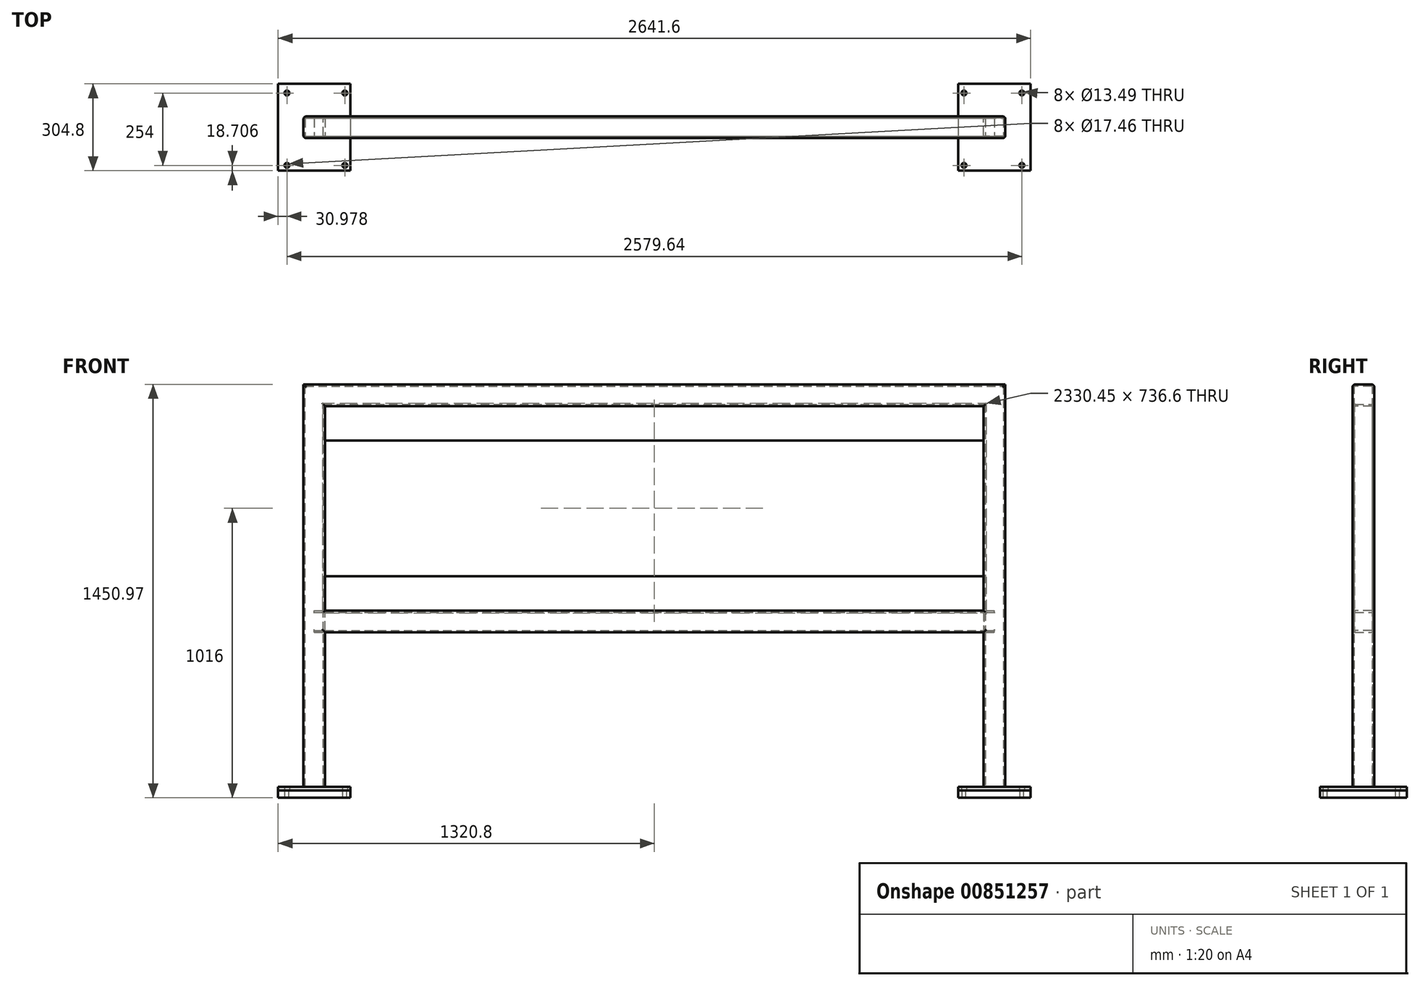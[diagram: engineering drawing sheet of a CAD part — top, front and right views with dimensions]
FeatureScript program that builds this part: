
annotation { "Feature Type Name" : "Feature", "Feature Type Description" : "" }
export const myFeature = defineFeature(function(context is Context, id is Id, definition is map)
    precondition{}
    {
        {
            var Q0;
            Q0=qCreatedBy(makeId("Top.planeOp"),FACE);
            var sketch = newSketch(context, id + "F0", { "sketchPlane" : qUnion([Q0])});
            skLineSegment(sketch, "E0", {"start": v(0, 315.7) * mm, "end": v(0, -421.09) * mm, "construction": true});
            skLineSegment(sketch, "E1", {"start": v(-1193.8, 0) * mm, "end": v(1193.8, 0) * mm, "construction": true});
            skLineSegment(sketch, "E2.0", {"start": v(-1193.8, 315.7) * mm, "end": v(-1193.8, -421.09) * mm, "construction": true});
            skPoint(sketch, "E3.orphan", {"position": v(-471.24, 0) * mm});
            skLineSegment(sketch, "E4.MirrorCS", {"start": v(1193.8, 315.7) * mm, "end": v(1193.8, -421.09) * mm, "construction": true});
            skLineSegment(sketch, "E5.bottom", {"start": v(-1320.8, 152.4) * mm, "end": v(-1066.8, 152.4) * mm});
            skLineSegment(sketch, "E5.top", {"start": v(-1320.8, -152.4) * mm, "end": v(-1066.8, -152.4) * mm});
            skLineSegment(sketch, "E5.left", {"start": v(-1320.8, 152.4) * mm, "end": v(-1320.8, -152.4) * mm});
            skLineSegment(sketch, "E5.right", {"start": v(-1066.8, 152.4) * mm, "end": v(-1066.8, -152.4) * mm});
            skPoint(sketch, "E5.middle", {"position": v(-1193.8, 0) * mm});
            skSolve(sketch);
        }
        {
            var Q0;
            Q0 = qSketchRegion(id + "F0", true);
            extrude(context, id + "F1", {"entities" : qUnion([Q0]), "depth" : 25.4 * mm, "offsetDistance" : 25.4 * mm});
        }
        {
            var Q0;
            Q0=makeQuery(id+"F1.opExtrude","CAP_FACE",FACE,{"disambiguationData":[OSD([sQuery(id+"F0.wireOp",EDGE,"E5.bottom"),sQuery(id+"F0.wireOp",EDGE,"E5.top"),sQuery(id+"F0.wireOp",EDGE,"E5.left"),sQuery(id+"F0.wireOp",EDGE,"E5.right")])],"isStart":false});
            var sketch = newSketch(context, id + "F2", { "sketchPlane" : qUnion([Q0])});
            skLineSegment(sketch, "E6", {"start": v(-1320.8, 152.4) * mm, "end": v(-1066.8, -152.4) * mm, "construction": true});
            skLineSegment(sketch, "E7.bottom", {"start": v(-1289.82, 120.3) * mm, "end": v(-1086.62, 120.3) * mm, "construction": true});
            skLineSegment(sketch, "E7.top", {"start": v(-1289.82, -133.7) * mm, "end": v(-1086.62, -133.7) * mm, "construction": true});
            skLineSegment(sketch, "E7.left", {"start": v(-1289.82, 120.3) * mm, "end": v(-1289.82, -133.7) * mm, "construction": true});
            skLineSegment(sketch, "E7.right", {"start": v(-1086.62, 120.3) * mm, "end": v(-1086.62, -133.7) * mm, "construction": true});
            skPoint(sketch, "E7.middle", {"position": v(-1188.22, -6.7) * mm});
            skPoint(sketch, "E8", {"position": v(-1289.82, 120.3) * mm});
            skPoint(sketch, "E9", {"position": v(-1086.62, 120.3) * mm});
            skPoint(sketch, "E10", {"position": v(-1289.82, -133.7) * mm});
            skPoint(sketch, "E11", {"position": v(-1086.62, -133.7) * mm});
            skSolve(sketch);
        }
        {
            var Q0;
            Q0=sQuery(id+"F2.wireOp",VERTEX,"E8");
            var Q1;
            Q1=sQuery(id+"F2.wireOp",VERTEX,"E9");
            var Q2;
            Q2=sQuery(id+"F2.wireOp",VERTEX,"E10");
            var Q3;
            Q3=sQuery(id+"F2.wireOp",VERTEX,"E11");
            var Q4;
            Q4=makeQuery(id+"F1.opExtrude","SWEPT_BODY",BODY,{"disambiguationData":[OSD([sQuery(id+"F0.wireOp",EDGE,"E5.bottom"),sQuery(id+"F0.wireOp",EDGE,"E5.top"),sQuery(id+"F0.wireOp",EDGE,"E5.left"),sQuery(id+"F0.wireOp",EDGE,"E5.right")])]});
            hole(context, id + "F3", {"style" : HoleStyle.SIMPLE, "endStyle" : HoleEndStyle.THROUGH, "standardTappedOrClearance" : lookupTablePath({ "standard" : "ANSI", "engagement" : "75%", "pitch" : "11 tpi", "size" : "5/8", "type" : "Tapped" }), "standardBlindInLast" : lookupTablePath({ "standard" : "ANSI", "engagement" : "75%", "pitch" : "11 tpi", "size" : "5/8", "type" : "Tapped" }), "holeDiameter" : 13.5 * mm, "majorDiameter" : 15.88 * mm, "showTappedDepth" : true, "isTappedThrough" : true, "tappedDepth" : 38.1 * mm, "tapClearance" : 3, "startFromSketch" : true, "locations" : qUnion([Q0, Q1, Q2, Q3]), "scope" : qUnion([Q4])});
        }
        {
            var Q0;
            Q0=makeQuery(id+"F1.opExtrude","CAP_FACE",FACE,{"disambiguationData":[OSD([sQuery(id+"F0.wireOp",EDGE,"E5.bottom"),sQuery(id+"F0.wireOp",EDGE,"E5.top"),sQuery(id+"F0.wireOp",EDGE,"E5.left"),sQuery(id+"F0.wireOp",EDGE,"E5.right")])],"isStart":false});
            var sketch = newSketch(context, id + "F4", { "sketchPlane" : qUnion([Q0])});
            skLineSegment(sketch, "E12.0", {"start": v(-1320.8, 152.4) * mm, "end": v(-1066.8, 152.4) * mm});
            skLineSegment(sketch, "E13.0", {"start": v(-1320.8, 152.4) * mm, "end": v(-1320.8, -152.4) * mm});
            skLineSegment(sketch, "E14.0", {"start": v(-1320.8, -152.4) * mm, "end": v(-1066.8, -152.4) * mm});
            skLineSegment(sketch, "E15.0", {"start": v(-1066.8, 152.4) * mm, "end": v(-1066.8, -152.4) * mm});
            skCircle(sketch, "E16.0", {"center": v(-1289.82, 120.3) * mm, "radius": 6.75 * mm, "construction": true});
            skCircle(sketch, "E17.0", {"center": v(-1086.62, 120.3) * mm, "radius": 6.75 * mm, "construction": true});
            skCircle(sketch, "E18.0", {"center": v(-1289.82, -133.7) * mm, "radius": 6.75 * mm, "construction": true});
            skCircle(sketch, "E19.0", {"center": v(-1086.62, -133.7) * mm, "radius": 6.75 * mm, "construction": true});
            skCircle(sketch, "E20", {"center": v(-1289.82, 120.3) * mm, "radius": 8.73 * mm});
            skCircle(sketch, "E21", {"center": v(-1086.62, 120.3) * mm, "radius": 8.73 * mm});
            skCircle(sketch, "E22", {"center": v(-1289.82, -133.7) * mm, "radius": 8.73 * mm});
            skCircle(sketch, "E23", {"center": v(-1086.62, -133.7) * mm, "radius": 8.73 * mm});
            skSolve(sketch);
        }
        {
            var Q0;
            Q0 = qSketchRegion(id + "F4", true);
            extrude(context, id + "F5", {"entities" : qUnion([Q0]), "depth" : 12.7 * mm, "offsetDistance" : 25.4 * mm});
        }
        {
            var Q0;
            Q0=makeQuery(id+"F5.opExtrude","SWEPT_BODY",BODY,{"disambiguationData":[OSD([sQuery(id+"F4.wireOp",EDGE,"E12.0"),sQuery(id+"F4.wireOp",EDGE,"E13.0"),sQuery(id+"F4.wireOp",EDGE,"E14.0"),sQuery(id+"F4.wireOp",EDGE,"E15.0"),sQuery(id+"F4.wireOp",EDGE,"E20"),sQuery(id+"F4.wireOp",EDGE,"E21"),sQuery(id+"F4.wireOp",EDGE,"E22"),sQuery(id+"F4.wireOp",EDGE,"E23")])]});
            var Q1;
            Q1=makeQuery(id+"F1.opExtrude","SWEPT_BODY",BODY,{"disambiguationData":[OSD([sQuery(id+"F0.wireOp",EDGE,"E5.bottom"),sQuery(id+"F0.wireOp",EDGE,"E5.top"),sQuery(id+"F0.wireOp",EDGE,"E5.left"),sQuery(id+"F0.wireOp",EDGE,"E5.right")])]});
            var Q2;
            Q2=qCreatedBy(makeId("Right.planeOp"),FACE);
            mirror(context, id + "F6", {"entities" : qUnion([Q0, Q1]), "mirrorPlane" : qUnion([Q2])});
        }
        {
            var Q0;
            Q0=qCreatedBy(makeId("Front.planeOp"),FACE);
            var sketch = newSketch(context, id + "F7", { "sketchPlane" : qUnion([Q0])});
            skLineSegment(sketch, "E24.0", {"start": v(-1320.8, 38.1) * mm, "end": v(-1066.8, 38.1) * mm, "construction": true});
            skLineSegment(sketch, "E25.0", {"start": v(1320.8, 38.1) * mm, "end": v(1066.8, 38.1) * mm, "construction": true});
            skLineSegment(sketch, "E26", {"start": v(-1193.8, 38.1) * mm, "end": v(-1193.8, 1412.88) * mm});
            skLineSegment(sketch, "E27", {"start": v(-1193.8, 1412.88) * mm, "end": v(1193.8, 1412.88) * mm});
            skPoint(sketch, "E27.endSnap0", {"position": v(1193.8, 38.1) * mm});
            skLineSegment(sketch, "E28", {"start": v(1193.8, 1412.88) * mm, "end": v(1193.8, 38.1) * mm});
            skLineSegment(sketch, "E29", {"start": v(1193.8, 581.03) * mm, "end": v(-1193.8, 581.02) * mm});
            skSolve(sketch);
        }
        {
            var Q0;
            Q0=makeQuery(id+"F5.opExtrude","CAP_FACE",FACE,{"disambiguationData":[OSD([sQuery(id+"F4.wireOp",EDGE,"E12.0"),sQuery(id+"F4.wireOp",EDGE,"E13.0"),sQuery(id+"F4.wireOp",EDGE,"E14.0"),sQuery(id+"F4.wireOp",EDGE,"E15.0"),sQuery(id+"F4.wireOp",EDGE,"E20"),sQuery(id+"F4.wireOp",EDGE,"E21"),sQuery(id+"F4.wireOp",EDGE,"E22"),sQuery(id+"F4.wireOp",EDGE,"E23")])],"isStart":false});
            var sketch = newSketch(context, id + "F8", { "sketchPlane" : qUnion([Q0])});
            skLineSegment(sketch, "E30.0", {"start": v(1193.8, 0) * mm, "end": v(-1193.8, 0) * mm, "construction": true});
            skLineSegment(sketch, "E31.bottom", {"start": v(-1222.38, 38.1) * mm, "end": v(-1165.23, 38.1) * mm});
            skLineSegment(sketch, "E31.top", {"start": v(-1222.38, -38.1) * mm, "end": v(-1165.23, -38.1) * mm});
            skLineSegment(sketch, "E31.left", {"start": v(-1231.9, 28.57) * mm, "end": v(-1231.9, -28.58) * mm});
            skLineSegment(sketch, "E31.right", {"start": v(-1155.7, 28.57) * mm, "end": v(-1155.7, -28.58) * mm});
            skPoint(sketch, "E31.middle", {"position": v(-1193.8, 0) * mm});
            skPoint(sketch, "E32.visualSharp", {"position": v(-1231.9, 38.1) * mm});
            skArc(sketch, "E32.filletArc", {"start": v(-1222.38, 38.1) * mm, "mid": v(-1229.11, 35.31) * mm, "end": v(-1231.9, 28.57) * mm});
            skPoint(sketch, "E33.visualSharp", {"position": v(-1155.7, 38.1) * mm});
            skArc(sketch, "E33.filletArc", {"start": v(-1155.7, 28.57) * mm, "mid": v(-1158.49, 35.31) * mm, "end": v(-1165.23, 38.1) * mm});
            skPoint(sketch, "E34.visualSharp", {"position": v(-1155.7, -38.1) * mm});
            skArc(sketch, "E34.filletArc", {"start": v(-1165.23, -38.1) * mm, "mid": v(-1158.49, -35.31) * mm, "end": v(-1155.7, -28.58) * mm});
            skPoint(sketch, "E35.visualSharp", {"position": v(-1231.9, -38.1) * mm});
            skArc(sketch, "E35.filletArc", {"start": v(-1231.9, -28.58) * mm, "mid": v(-1229.11, -35.31) * mm, "end": v(-1222.38, -38.1) * mm});
            skArc(sketch, "E36.0", {"start": v(-1222.38, 31.75) * mm, "mid": v(-1224.62, 30.82) * mm, "end": v(-1225.55, 28.57) * mm});
            skLineSegment(sketch, "E36.1", {"start": v(-1225.55, 28.57) * mm, "end": v(-1225.55, -28.58) * mm});
            skLineSegment(sketch, "E36.2", {"start": v(-1222.38, 31.75) * mm, "end": v(-1165.23, 31.75) * mm});
            skArc(sketch, "E36.3", {"start": v(-1225.55, -28.58) * mm, "mid": v(-1224.62, -30.82) * mm, "end": v(-1222.38, -31.75) * mm});
            skArc(sketch, "E36.4", {"start": v(-1162.05, 28.57) * mm, "mid": v(-1162.98, 30.82) * mm, "end": v(-1165.23, 31.75) * mm});
            skLineSegment(sketch, "E36.5", {"start": v(-1162.05, 28.57) * mm, "end": v(-1162.05, -28.58) * mm});
            skArc(sketch, "E36.6", {"start": v(-1165.23, -31.75) * mm, "mid": v(-1162.98, -30.82) * mm, "end": v(-1162.05, -28.58) * mm});
            skLineSegment(sketch, "E36.7", {"start": v(-1222.38, -31.75) * mm, "end": v(-1165.23, -31.75) * mm});
            skSolve(sketch);
        }
        {
            var Q0;
            Q0=makeQuery(id+"F8.imprint","IMPRINT",FACE,{"disambiguationData":[TD([[makeQuery(id+"F8.imprint","IMPRINT",EDGE,{"derivedFrom":sQuery(id+"F8.wireOp",EDGE,"E31.bottom")}),-1.0]])]});
            var Q1;
            Q1=sQuery(id+"F7.wireOp",EDGE,"E26");
            var Q2;
            Q2=sQuery(id+"F7.wireOp",EDGE,"E27");
            var Q3;
            Q3=sQuery(id+"F7.wireOp",EDGE,"E28");
            sweep(context, id + "F9", {"profiles" : qUnion([Q0]), "path" : qUnion([Q1, Q2, Q3])});
        }
        {
            var Q0;
            Q0=makeQuery(id+"F9.opSweep","SWEPT_FACE",FACE,{"disambiguationData":[OSD([sQuery(id+"F7.wireOp",EDGE,"E26"),sQuery(id+"F8.wireOp",EDGE,"E31.right")])]});
            var sketch = newSketch(context, id + "F10", { "sketchPlane" : qUnion([Q0])});
            skLineSegment(sketch, "E37.0", {"start": v(-28.58, 619.12) * mm, "end": v(28.57, 619.12) * mm, "construction": true});
            skLineSegment(sketch, "E38.bottom", {"start": v(28.57, 657.23) * mm, "end": v(-28.58, 657.23) * mm});
            skLineSegment(sketch, "E38.top", {"start": v(28.57, 581.02) * mm, "end": v(-28.58, 581.02) * mm});
            skLineSegment(sketch, "E38.left", {"start": v(38.1, 647.7) * mm, "end": v(38.1, 590.55) * mm});
            skLineSegment(sketch, "E38.right", {"start": v(-38.1, 647.7) * mm, "end": v(-38.1, 590.55) * mm});
            skPoint(sketch, "E38.middle", {"position": v(0, 619.12) * mm});
            skPoint(sketch, "E39.visualSharp", {"position": v(38.1, 657.23) * mm});
            skArc(sketch, "E39.filletArc", {"start": v(38.1, 647.7) * mm, "mid": v(35.31, 654.44) * mm, "end": v(28.57, 657.23) * mm});
            skPoint(sketch, "E40.visualSharp", {"position": v(38.1, 581.02) * mm});
            skArc(sketch, "E40.filletArc", {"start": v(28.57, 581.02) * mm, "mid": v(35.31, 583.81) * mm, "end": v(38.1, 590.55) * mm});
            skPoint(sketch, "E41.visualSharp", {"position": v(-38.1, 581.02) * mm});
            skArc(sketch, "E41.filletArc", {"start": v(-38.1, 590.55) * mm, "mid": v(-35.31, 583.81) * mm, "end": v(-28.58, 581.02) * mm});
            skPoint(sketch, "E42.visualSharp", {"position": v(-38.1, 657.23) * mm});
            skArc(sketch, "E42.filletArc", {"start": v(-28.58, 657.23) * mm, "mid": v(-35.31, 654.44) * mm, "end": v(-38.1, 647.7) * mm});
            skArc(sketch, "E43.0", {"start": v(31.75, 647.7) * mm, "mid": v(30.82, 649.95) * mm, "end": v(28.57, 650.88) * mm});
            skLineSegment(sketch, "E43.1", {"start": v(28.57, 650.88) * mm, "end": v(-28.58, 650.88) * mm});
            skLineSegment(sketch, "E43.2", {"start": v(31.75, 647.7) * mm, "end": v(31.75, 590.55) * mm});
            skArc(sketch, "E43.3", {"start": v(-28.58, 650.88) * mm, "mid": v(-30.82, 649.95) * mm, "end": v(-31.75, 647.7) * mm});
            skArc(sketch, "E43.4", {"start": v(28.57, 587.38) * mm, "mid": v(30.82, 588.3) * mm, "end": v(31.75, 590.55) * mm});
            skLineSegment(sketch, "E43.5", {"start": v(28.57, 587.38) * mm, "end": v(-28.58, 587.38) * mm});
            skArc(sketch, "E43.6", {"start": v(-31.75, 590.55) * mm, "mid": v(-30.82, 588.3) * mm, "end": v(-28.58, 587.38) * mm});
            skLineSegment(sketch, "E43.7", {"start": v(-31.75, 647.7) * mm, "end": v(-31.75, 590.55) * mm});
            skSolve(sketch);
        }
        {
            var Q0;
            {var subQ0=sQuery(id+"F10.wireOp",EDGE,"E38.top");Q0=makeQuery(id+"F10.imprint","IMPRINT",FACE,{"disambiguationData":[TD([[makeQuery(id+"F10.imprint","IMPRINT",EDGE,{"derivedFrom":subQ0}),-1.0]])]});}
            var Q1;
            Q1=makeQuery(id+"F10.imprint","IMPRINT",FACE,{"disambiguationData":[TD([[makeQuery(id+"F10.imprint","IMPRINT",EDGE,{"derivedFrom":sQuery(id+"F10.wireOp",EDGE,"E38.right")}),1.0]])]});
            var Q2;
            {var subQ0=sQuery(id+"F10.wireOp",EDGE,"E38.bottom");Q2=makeQuery(id+"F10.imprint","IMPRINT",FACE,{"disambiguationData":[TD([[makeQuery(id+"F10.imprint","IMPRINT",EDGE,{"derivedFrom":subQ0}),1.0]])]});}
            var Q3;
            Q3=makeQuery(id+"F10.imprint","IMPRINT",FACE,{"disambiguationData":[TD([[makeQuery(id+"F10.imprint","IMPRINT",EDGE,{"derivedFrom":sQuery(id+"F10.wireOp",EDGE,"E38.left")}),-1.0]])]});
            var Q4;
            Q4=sQuery(id+"F7.wireOp",EDGE,"E29");
            sweep(context, id + "F11", {"operationType" : NewBodyOperationType.ADD, "profiles" : qUnion([Q0, Q1, Q2, Q3]), "path" : qUnion([Q4])});
        }
        {
            var Q0;
            Q0=makeQuery(id+"F11.boolean.opBoolean","MERGE",FACE,{"derivedFrom":[makeQuery(id+"F9.opSweep","SWEPT_FACE",FACE,{"disambiguationData":[OSD([sQuery(id+"F7.wireOp",EDGE,"E26"),sQuery(id+"F8.wireOp",EDGE,"E31.bottom")])]}),makeQuery(id+"F11.opSweep","SWEPT_FACE",FACE,{"disambiguationData":[OSD([sQuery(id+"F7.wireOp",EDGE,"E29"),sQuery(id+"F10.wireOp",EDGE,"E38.left")])]})]});
            var sketch = newSketch(context, id + "F12", { "sketchPlane" : qUnion([Q0])});
            skLineSegment(sketch, "E44.0.1", {"start": v(-1155.7, 657.23) * mm, "end": v(-1155.7, 1374.77) * mm, "construction": true});
            skLineSegment(sketch, "E44.0.3", {"start": v(-1155.7, 1374.77) * mm, "end": v(-1155.7, 657.23) * mm, "construction": true});
            skLineSegment(sketch, "E45.0", {"start": v(1155.7, 1374.77) * mm, "end": v(-1155.7, 1374.77) * mm, "construction": true});
            skLineSegment(sketch, "E46.0", {"start": v(1155.7, 657.23) * mm, "end": v(1155.7, 1374.78) * mm, "construction": true});
            skLineSegment(sketch, "E47.0", {"start": v(1155.7, 657.23) * mm, "end": v(-1155.7, 657.23) * mm, "construction": true});
            skLineSegment(sketch, "E48.bottom", {"start": v(-1155.7, 1374.77) * mm, "end": v(1155.7, 1374.77) * mm});
            skLineSegment(sketch, "E48.top", {"start": v(-1155.7, 1254.12) * mm, "end": v(1155.7, 1254.12) * mm});
            skLineSegment(sketch, "E48.left", {"start": v(-1155.7, 1374.77) * mm, "end": v(-1155.7, 1254.12) * mm});
            skLineSegment(sketch, "E48.right", {"start": v(1155.7, 1374.77) * mm, "end": v(1155.7, 1254.12) * mm});
            skLineSegment(sketch, "E49.bottom", {"start": v(-1155.7, 657.23) * mm, "end": v(1155.7, 657.23) * mm});
            skLineSegment(sketch, "E49.top", {"start": v(-1155.7, 777.88) * mm, "end": v(1155.7, 777.88) * mm});
            skLineSegment(sketch, "E49.left", {"start": v(-1155.7, 657.23) * mm, "end": v(-1155.7, 777.88) * mm});
            skLineSegment(sketch, "E49.right", {"start": v(1155.7, 657.23) * mm, "end": v(1155.7, 777.88) * mm});
            skSolve(sketch);
        }
        {
            var Q0;
            Q0=makeQuery(id+"F12.imprint","IMPRINT",FACE,{"disambiguationData":[TD([[makeQuery(id+"F12.imprint","IMPRINT",EDGE,{"derivedFrom":sQuery(id+"F12.wireOp",EDGE,"E48.bottom")}),-1.0]])]});
            var Q1;
            Q1=makeQuery(id+"F12.imprint","IMPRINT",FACE,{"disambiguationData":[TD([[makeQuery(id+"F12.imprint","IMPRINT",EDGE,{"derivedFrom":sQuery(id+"F12.wireOp",EDGE,"E49.bottom")}),1.0]])]});
            extrude(context, id + "F13", {"entities" : qUnion([Q0, Q1]), "oppositeDirection" : true, "depth" : 6.35 * mm, "offsetDistance" : 25.4 * mm});
        }
    });
